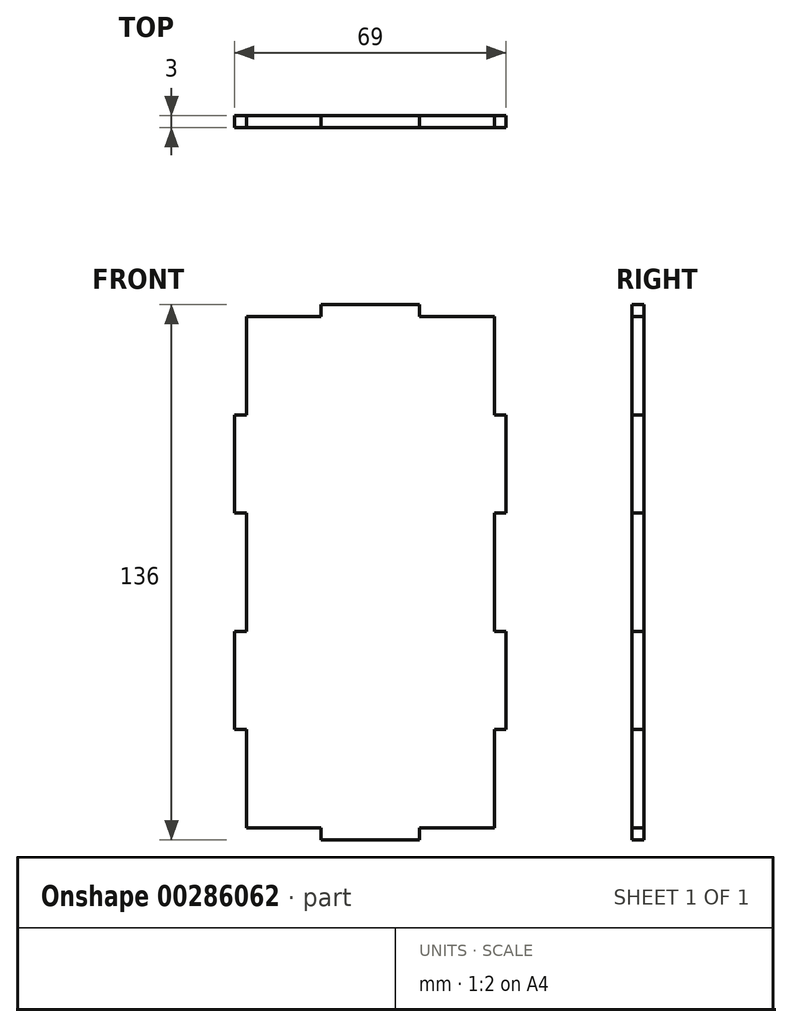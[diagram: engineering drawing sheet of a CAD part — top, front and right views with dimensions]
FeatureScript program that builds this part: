
annotation { "Feature Type Name" : "Feature", "Feature Type Description" : "" }
export const myFeature = defineFeature(function(context is Context, id is Id, definition is map)
    precondition{}
    {
        {
            var Q0;
            Q0=qCreatedBy(makeId("Front.planeOp"),FACE);
            var sketch = newSketch(context, id + "F0", { "sketchPlane" : qUnion([Q0])});
            skLineSegment(sketch, "E0.bottom", {"start": v(0, 0) * mm, "end": v(-31.5, 0) * mm, "construction": true});
            skLineSegment(sketch, "E0.top", {"start": v(0, 65) * mm, "end": v(-31.5, 65) * mm, "construction": true});
            skLineSegment(sketch, "E0.left", {"start": v(0, 0) * mm, "end": v(0, 65) * mm, "construction": true});
            skLineSegment(sketch, "E0.right", {"start": v(-31.5, 0) * mm, "end": v(-31.5, 65) * mm, "construction": true});
            skLineSegment(sketch, "E1", {"start": v(-31.5, 40) * mm, "end": v(-34.5, 40) * mm});
            skLineSegment(sketch, "E2", {"start": v(-12.5, 65) * mm, "end": v(-12.5, 68) * mm});
            skLineSegment(sketch, "E3", {"start": v(-12.5, 68) * mm, "end": v(0, 68) * mm});
            skLineSegment(sketch, "E4", {"start": v(-34.5, 40) * mm, "end": v(-34.5, 15) * mm});
            skLineSegment(sketch, "E5", {"start": v(-34.5, 15) * mm, "end": v(-31.5, 15) * mm});
            skLineSegment(sketch, "E6", {"start": v(-31.5, 15) * mm, "end": v(-31.5, 0) * mm});
            skLineSegment(sketch, "E7.MirrorCS", {"start": v(-31.5, -40) * mm, "end": v(-34.5, -40) * mm});
            skLineSegment(sketch, "E8.MirrorCS", {"start": v(-12.5, -65) * mm, "end": v(-12.5, -68) * mm});
            skLineSegment(sketch, "E9.MirrorCS", {"start": v(-34.5, -15) * mm, "end": v(-31.5, -15) * mm});
            skLineSegment(sketch, "E10.MirrorCS", {"start": v(0, -65) * mm, "end": v(-31.5, -65) * mm, "construction": true});
            skLineSegment(sketch, "E11.MirrorCS", {"start": v(-34.5, -40) * mm, "end": v(-34.5, -15) * mm});
            skLineSegment(sketch, "E12.MirrorCS", {"start": v(-12.5, -68) * mm, "end": v(0, -68) * mm});
            skLineSegment(sketch, "E13.MirrorCS", {"start": v(-31.5, 0) * mm, "end": v(-31.5, -65) * mm, "construction": true});
            skLineSegment(sketch, "E14.MirrorCS", {"start": v(0, 0) * mm, "end": v(0, -65) * mm, "construction": true});
            skLineSegment(sketch, "E15.MirrorCS", {"start": v(-31.5, -15) * mm, "end": v(-31.5, 0) * mm});
            skLineSegment(sketch, "E16.MirrorCS", {"start": v(12.5, -65) * mm, "end": v(12.5, -68) * mm});
            skLineSegment(sketch, "E17.MirrorCS", {"start": v(34.5, -15) * mm, "end": v(31.5, -15) * mm});
            skLineSegment(sketch, "E18.MirrorCS", {"start": v(34.5, 15) * mm, "end": v(31.5, 15) * mm});
            skLineSegment(sketch, "E19.MirrorCS", {"start": v(12.5, 65) * mm, "end": v(12.5, 68) * mm});
            skLineSegment(sketch, "E20.MirrorCS", {"start": v(31.5, 40) * mm, "end": v(34.5, 40) * mm});
            skLineSegment(sketch, "E21.MirrorCS", {"start": v(0, 0) * mm, "end": v(31.5, 0) * mm, "construction": true});
            skLineSegment(sketch, "E22.MirrorCS", {"start": v(31.5, -40) * mm, "end": v(34.5, -40) * mm});
            skLineSegment(sketch, "E23.MirrorCS", {"start": v(34.5, -40) * mm, "end": v(34.5, -15) * mm});
            skLineSegment(sketch, "E24.MirrorCS", {"start": v(12.5, -68) * mm, "end": v(0, -68) * mm});
            skLineSegment(sketch, "E25.MirrorCS", {"start": v(34.5, 40) * mm, "end": v(34.5, 15) * mm});
            skLineSegment(sketch, "E26.MirrorCS", {"start": v(31.5, 0) * mm, "end": v(31.5, -65) * mm, "construction": true});
            skLineSegment(sketch, "E27.MirrorCS", {"start": v(12.5, 68) * mm, "end": v(0, 68) * mm});
            skLineSegment(sketch, "E28.MirrorCS", {"start": v(31.5, -15) * mm, "end": v(31.5, 0) * mm});
            skLineSegment(sketch, "E29.MirrorCS", {"start": v(31.5, 15) * mm, "end": v(31.5, 0) * mm});
            skLineSegment(sketch, "E30.MirrorCS", {"start": v(31.5, 0) * mm, "end": v(31.5, 65) * mm, "construction": true});
            skLineSegment(sketch, "E31.MirrorCS", {"start": v(0, -65) * mm, "end": v(31.5, -65) * mm, "construction": true});
            skLineSegment(sketch, "E32.MirrorCS", {"start": v(0, 65) * mm, "end": v(31.5, 65) * mm, "construction": true});
            skLineSegment(sketch, "E33", {"start": v(-31.5, 40) * mm, "end": v(-31.5, 65) * mm});
            skLineSegment(sketch, "E34", {"start": v(12.5, 65) * mm, "end": v(31.5, 65) * mm});
            skLineSegment(sketch, "E35", {"start": v(31.5, 40) * mm, "end": v(31.5, 65) * mm});
            skLineSegment(sketch, "E36", {"start": v(-31.5, 65) * mm, "end": v(-12.5, 65) * mm});
            skLineSegment(sketch, "E37", {"start": v(-31.5, -40) * mm, "end": v(-31.5, -65) * mm});
            skLineSegment(sketch, "E38", {"start": v(-31.5, -65) * mm, "end": v(-12.5, -65) * mm});
            skLineSegment(sketch, "E39", {"start": v(12.5, -65) * mm, "end": v(31.5, -65) * mm});
            skLineSegment(sketch, "E40", {"start": v(31.5, -65) * mm, "end": v(31.5, -40) * mm});
            skSolve(sketch);
        }
        {
            var Q0;
            Q0=makeQuery(id+"F0.imprint","IMPRINT",FACE,{"disambiguationData":[TD([[makeQuery(id+"F0.imprint","IMPRINT",EDGE,{"derivedFrom":sQuery(id+"F0.wireOp",EDGE,"E1")}),1.0]])]});
            extrude(context, id + "F1", {"entities" : qUnion([Q0]), "depth" : 3 * mm});
        }
    });
